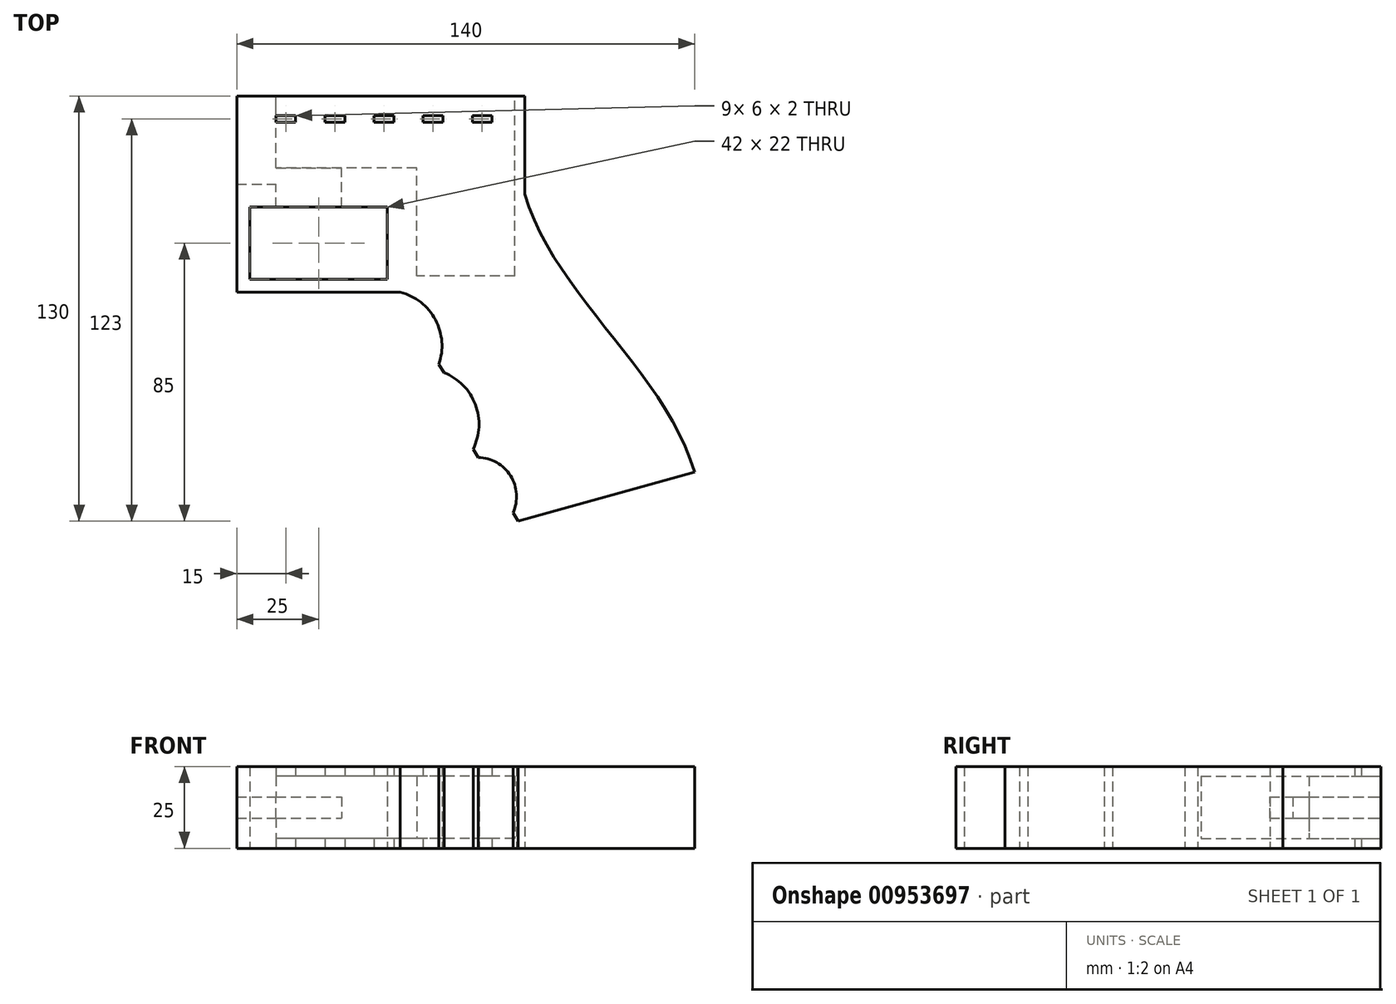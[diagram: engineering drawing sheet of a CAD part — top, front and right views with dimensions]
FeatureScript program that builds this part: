
annotation { "Feature Type Name" : "Feature", "Feature Type Description" : "" }
export const myFeature = defineFeature(function(context is Context, id is Id, definition is map)
    precondition{}
    {
        {
            var Q0;
            Q0=qCreatedBy(makeId("Top.planeOp"),FACE);
            var sketch = newSketch(context, id + "F0", { "sketchPlane" : qUnion([Q0])});
            skLineSegment(sketch, "E0.bottom", {"start": v(-44, 30) * mm, "end": v(44, 30) * mm});
            skLineSegment(sketch, "E0.top", {"start": v(-44, -30) * mm, "end": v(44, -30) * mm});
            skLineSegment(sketch, "E0.left", {"start": v(-44, 30) * mm, "end": v(-44, -30) * mm});
            skLineSegment(sketch, "E0.right", {"start": v(44, 30) * mm, "end": v(44, -30) * mm});
            skPoint(sketch, "E0.middle", {"position": v(0, 0) * mm});
            skLineSegment(sketch, "E1.bottom", {"start": v(-40, -26) * mm, "end": v(2, -26) * mm});
            skLineSegment(sketch, "E1.top", {"start": v(-40, -4) * mm, "end": v(2, -4) * mm});
            skLineSegment(sketch, "E1.left", {"start": v(-40, -26) * mm, "end": v(-40, -4) * mm});
            skLineSegment(sketch, "E1.right", {"start": v(2, -26) * mm, "end": v(2, -4) * mm});
            skLineSegment(sketch, "E2.bottom", {"start": v(-32, 24) * mm, "end": v(-26, 24) * mm});
            skLineSegment(sketch, "E2.top", {"start": v(-32, 22) * mm, "end": v(-26, 22) * mm});
            skLineSegment(sketch, "E2.left", {"start": v(-32, 24) * mm, "end": v(-32, 22) * mm});
            skLineSegment(sketch, "E2.right", {"start": v(-26, 24) * mm, "end": v(-26, 22) * mm});
            skLineSegment(sketch, "E3.1.0.0", {"start": v(-17, 22) * mm, "end": v(-11, 22) * mm});
            skLineSegment(sketch, "E3.1.0.1", {"start": v(-11, 24) * mm, "end": v(-11, 22) * mm});
            skLineSegment(sketch, "E3.1.0.2", {"start": v(-17, 24) * mm, "end": v(-11, 24) * mm});
            skLineSegment(sketch, "E3.1.0.3", {"start": v(-17, 24) * mm, "end": v(-17, 22) * mm});
            skLineSegment(sketch, "E3.2.0.0", {"start": v(-2, 22) * mm, "end": v(4, 22) * mm});
            skLineSegment(sketch, "E3.2.0.1", {"start": v(4, 24) * mm, "end": v(4, 22) * mm});
            skLineSegment(sketch, "E3.2.0.2", {"start": v(-2, 24) * mm, "end": v(4, 24) * mm});
            skLineSegment(sketch, "E3.2.0.3", {"start": v(-2, 24) * mm, "end": v(-2, 22) * mm});
            skLineSegment(sketch, "E3.direction1", {"start": v(-32, 22) * mm, "end": v(-17, 22) * mm, "construction": true});
            skLineSegment(sketch, "E4.0.3.0", {"start": v(13, 22) * mm, "end": v(19, 22) * mm});
            skLineSegment(sketch, "E4.3.3.0", {"start": v(19, 24) * mm, "end": v(19, 22) * mm});
            skLineSegment(sketch, "E4.6.3.0", {"start": v(13, 24) * mm, "end": v(19, 24) * mm});
            skLineSegment(sketch, "E4.9.3.0", {"start": v(13, 24) * mm, "end": v(13, 22) * mm});
            skLineSegment(sketch, "E4.0.4.0", {"start": v(28, 22) * mm, "end": v(34, 22) * mm});
            skLineSegment(sketch, "E4.3.4.0", {"start": v(34, 24) * mm, "end": v(34, 22) * mm});
            skLineSegment(sketch, "E4.6.4.0", {"start": v(28, 24) * mm, "end": v(34, 24) * mm});
            skLineSegment(sketch, "E4.9.4.0", {"start": v(28, 24) * mm, "end": v(28, 22) * mm});
            skFitSpline(sketch, "E5", {"points": [v(44, 0) * mm, v(96, -85) * mm], "startDerivative": vector(28.04, -93.29) * mm, "endDerivative": vector(28.04, -93.29) * mm});
            skLineSegment(sketch, "E6", {"start": v(96, -85) * mm, "end": v(42.05, -100) * mm});
            skLineSegment(sketch, "E7", {"start": v(42.05, -100) * mm, "end": v(40.45, -97.46) * mm});
            skArc(sketch, "E8", {"start": v(40.45, -97.46) * mm, "mid": v(39.7, -86.14) * mm, "end": v(29.85, -80.5) * mm});
            skLineSegment(sketch, "E9", {"start": v(29.85, -80.5) * mm, "end": v(28.25, -77.96) * mm});
            skArc(sketch, "E10", {"start": v(28.25, -77.96) * mm, "mid": v(28.94, -64.33) * mm, "end": v(19.38, -54.59) * mm});
            skLineSegment(sketch, "E11", {"start": v(19.38, -54.59) * mm, "end": v(17.79, -52.05) * mm});
            skArc(sketch, "E12", {"start": v(17.79, -52.05) * mm, "mid": v(16.72, -38.44) * mm, "end": v(6, -30) * mm});
            skSolve(sketch);
        }
        {
            var Q0;
            {var subQ5=sQuery(id+"F0.wireOp",EDGE,"E0.bottom");Q0=makeQuery(id+"F0.imprint","IMPRINT",FACE,{"disambiguationData":[TD([[makeQuery(id+"F0.imprint","IMPRINT",EDGE,{"derivedFrom":subQ5}),-1.0]])]});}
            var Q1;
            {var subQ0=sQuery(id+"F0.wireOp",EDGE,"E5");Q1=makeQuery(id+"F0.imprint","IMPRINT",FACE,{"disambiguationData":[TD([[makeQuery(id+"F0.imprint","IMPRINT",EDGE,{"derivedFrom":subQ0}),-1.0]])]});}
            extrude(context, id + "F1", {"entities" : qUnion([Q0, Q1]), "depth" : 25 * mm, "offsetDistance" : 25 * mm});
        }
        {
            var Q0;
            Q0=makeQuery(id+"F1.opExtrude","SWEPT_FACE",FACE,{"disambiguationData":[OSD([sQuery(id+"F0.wireOp",EDGE,"E0.bottom")])]});
            var sketch = newSketch(context, id + "F2", { "sketchPlane" : qUnion([Q0])});
            skLineSegment(sketch, "E13.bottom", {"start": v(-41, 22) * mm, "end": v(32, 22) * mm});
            skLineSegment(sketch, "E13.top", {"start": v(-41, 3) * mm, "end": v(32, 3) * mm});
            skLineSegment(sketch, "E13.left", {"start": v(-41, 22) * mm, "end": v(-41, 3) * mm});
            skLineSegment(sketch, "E13.right", {"start": v(32, 22) * mm, "end": v(32, 3) * mm});
            skLineSegment(sketch, "E14", {"start": v(-11, 22) * mm, "end": v(-11, 3) * mm});
            skLineSegment(sketch, "E15.bottom", {"start": v(44, 15.75) * mm, "end": v(12, 15.75) * mm});
            skLineSegment(sketch, "E15.top", {"start": v(44, 9.25) * mm, "end": v(12, 9.25) * mm});
            skLineSegment(sketch, "E15.left", {"start": v(44, 15.75) * mm, "end": v(44, 9.25) * mm});
            skLineSegment(sketch, "E15.right", {"start": v(12, 15.75) * mm, "end": v(12, 9.25) * mm});
            skLineSegment(sketch, "E16", {"start": v(25.77, 15.75) * mm, "end": v(25.77, 22) * mm, "construction": true});
            skLineSegment(sketch, "E17", {"start": v(25.77, 9.25) * mm, "end": v(25.77, 3) * mm, "construction": true});
            skSolve(sketch);
        }
        {
            var Q0;
            {var subQ0=sQuery(id+"F2.wireOp",EDGE,"E13.left");Q0=makeQuery(id+"F2.imprint","IMPRINT",FACE,{"disambiguationData":[TD([[makeQuery(id+"F2.imprint","IMPRINT",EDGE,{"derivedFrom":subQ0}),1.0]])]});}
            var Q1;
            {var subQ9=sQuery(id+"F2.wireOp",EDGE,"E14");Q1=makeQuery(id+"F2.imprint","IMPRINT",FACE,{"disambiguationData":[TD([[makeQuery(id+"F2.imprint","IMPRINT",EDGE,{"derivedFrom":subQ9}),1.0]])]});}
            var Q2;
            {var subQ5=sQuery(id+"F2.wireOp",EDGE,"E15.right");Q2=makeQuery(id+"F2.imprint","IMPRINT",FACE,{"disambiguationData":[TD([[makeQuery(id+"F2.imprint","IMPRINT",EDGE,{"derivedFrom":subQ5}),1.0]])]});}
            var Q3;
            {var subQ5=sQuery(id+"F2.wireOp",EDGE,"E15.left");Q3=makeQuery(id+"F2.imprint","IMPRINT",FACE,{"disambiguationData":[TD([[makeQuery(id+"F2.imprint","IMPRINT",EDGE,{"derivedFrom":subQ5}),-1.0]])]});}
            extrude(context, id + "F3", {"entities" : qUnion([Q0, Q1, Q2, Q3]), "operationType" : NewBodyOperationType.REMOVE, "oppositeDirection" : true, "depth" : 22 * mm, "offsetDistance" : 25 * mm});
        }
        {
            var Q0;
            {var subQ0=sQuery(id+"F2.wireOp",EDGE,"E13.left");Q0=makeQuery(id+"F2.imprint","IMPRINT",FACE,{"disambiguationData":[TD([[makeQuery(id+"F2.imprint","IMPRINT",EDGE,{"derivedFrom":subQ0}),1.0]])]});}
            extrude(context, id + "F4", {"entities" : qUnion([Q0]), "operationType" : NewBodyOperationType.REMOVE, "oppositeDirection" : true, "depth" : 55 * mm, "offsetDistance" : 25 * mm});
        }
        {
            var Q0;
            {var subQ5=sQuery(id+"F2.wireOp",EDGE,"E15.right");Q0=makeQuery(id+"F2.imprint","IMPRINT",FACE,{"disambiguationData":[TD([[makeQuery(id+"F2.imprint","IMPRINT",EDGE,{"derivedFrom":subQ5}),1.0]])]});}
            var Q1;
            Q1=makeQuery(id+"F1.opExtrude","SWEPT_FACE",FACE,{"disambiguationData":[OSD([sQuery(id+"F0.wireOp",EDGE,"E1.top")])]});
            extrude(context, id + "F5", {"entities" : qUnion([Q0]), "operationType" : NewBodyOperationType.REMOVE, "endBound" : BoundingType.UP_TO_SURFACE, "oppositeDirection" : true, "depth" : 25 * mm, "endBoundEntityFace" : qUnion([Q1]), "offsetDistance" : 25 * mm});
        }
        {
            var Q0;
            {var subQ5=sQuery(id+"F2.wireOp",EDGE,"E15.left");Q0=makeQuery(id+"F2.imprint","IMPRINT",FACE,{"disambiguationData":[TD([[makeQuery(id+"F2.imprint","IMPRINT",EDGE,{"derivedFrom":subQ5}),-1.0]])]});}
            extrude(context, id + "F6", {"entities" : qUnion([Q0]), "operationType" : NewBodyOperationType.REMOVE, "oppositeDirection" : true, "depth" : 27 * mm, "offsetDistance" : 25 * mm});
        }
    });
